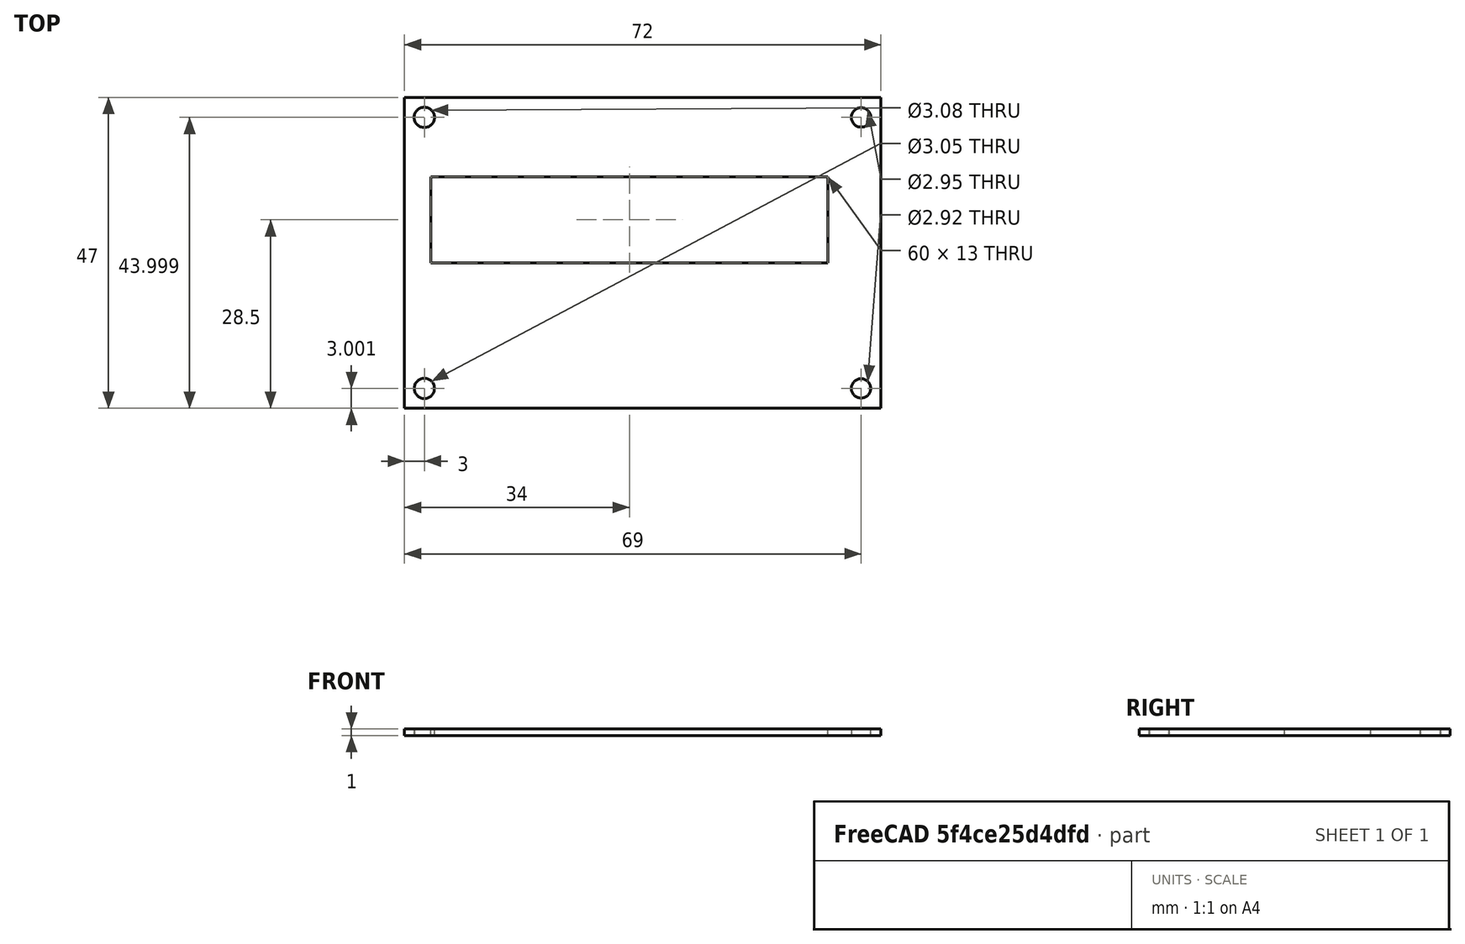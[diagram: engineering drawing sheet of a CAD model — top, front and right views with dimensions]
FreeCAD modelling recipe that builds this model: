
FCSTD DOCUMENT  (FreeCAD 0.18R16161 (Git))
Label: displayTest
License: All rights reserved
LicenseURL: http://en.wikipedia.org/wiki/All_rights_reserved
objects: App::MeasureDistance×2, Sketcher::SketchObject×1, PartDesign::Pad×1, PartDesign::Body×1
note: 4 computed .brp shape members not serialized (recipe doc carries the construction recipe); baked Part::Feature solids carry a one-line shape summary decoded from their .brp

FEATURE [Sketcher::SketchObject] Sketch
  MapMode = 5
  Support = -> [XY_Plane]
  sketch-geometry (12):
    g0: LineSegment StartX=-36 StartY=23.5 StartZ=0 EndX=36 EndY=23.5 EndZ=0
    g1: LineSegment StartX=36 StartY=23.5 StartZ=0 EndX=36 EndY=-23.5 EndZ=0
    g2: LineSegment StartX=36 StartY=-23.5 StartZ=0 EndX=-36 EndY=-23.5 EndZ=0
    g3: LineSegment StartX=-36 StartY=-23.5 StartZ=0 EndX=-36 EndY=23.5 EndZ=0
    g4: LineSegment StartX=-32 StartY=-1.5 StartZ=0 EndX=28 EndY=-1.5 EndZ=0
    g5: LineSegment StartX=28 StartY=-1.5 StartZ=0 EndX=28 EndY=11.5 EndZ=0
    g6: LineSegment StartX=28 StartY=11.5 StartZ=0 EndX=-32 EndY=11.5 EndZ=0
    g7: LineSegment StartX=-32 StartY=11.5 StartZ=0 EndX=-32 EndY=-1.5 EndZ=0
    g8: Circle CenterX=-33 CenterY=-20.4994 CenterZ=0 NormalX=0 NormalY=0 NormalZ=1 AngleXU=0 Radius=1.52607
    g9: Circle CenterX=-33 CenterY=20.4994 CenterZ=0 NormalX=0 NormalY=0 NormalZ=1 AngleXU=0 Radius=1.53903
    g10: Circle CenterX=33 CenterY=20.4994 CenterZ=0 NormalX=0 NormalY=0 NormalZ=1 AngleXU=0 Radius=1.47578
    g11: Circle CenterX=33 CenterY=-20.4994 CenterZ=0 NormalX=0 NormalY=0 NormalZ=1 AngleXU=0 Radius=1.45982
  constraints (16):
    c: Coincident(g0,g1)
    c: Coincident(g1,g2)
    c: Coincident(g2,g3)
    c: Coincident(g3,g0)
    c: Horizontal(g0)
    c: Horizontal(g2)
    c: Vertical(g1)
    c: Vertical(g3)
    c: Coincident(g4,g5)
    c: Coincident(g5,g6)
    c: Coincident(g6,g7)
    c: Coincident(g7,g4)
    c: Horizontal(g4)
    c: Horizontal(g6)
    c: Vertical(g5)
    c: Vertical(g7)
FEATURE [PartDesign::Pad] Pad
  Length = 1
  Length2 = 100
  Profile = -> Sketch
  Type = 0
FEATURE [PartDesign::Body] Body
  Group = -> [Sketch,Pad]
  Origin = -> Origin
  Tip = -> Pad
FEATURE [App::MeasureDistance] Distance  label="Distance: 12.00 mm"
  Distance = 12.0005
  P1 = (-27.9561,23.5,1)
  P2 = (-28.0631,11.5,1)
FEATURE [App::MeasureDistance] Distance001  label="Distance: 4.00 mm"
  Distance = 4.00043
  P1 = (-32,8.61974,1)
  P2 = (-36,8.56137,1)
